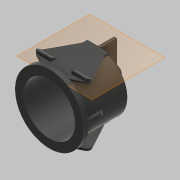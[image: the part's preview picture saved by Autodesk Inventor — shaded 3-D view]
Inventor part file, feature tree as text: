
AUTODESK INVENTOR PART (.ipt)
format: ipt  version: 2018.1 (Build 221171000, 171)  size: 242,688 bytes
history: native  units: mm
features: extrude x7, sketch x7, chamfer x3, other x2, mirror x1, projected_geometry x1
ambient origin geometry x8: Origin, YZ Plane, XZ Plane, XY Plane, X Axis, Y Axis, Z Axis, Center Point
bodies: body (feature_tree)
feature tree (21):
  other  "Твердое тело1"
  extrude  "Выдавливание1"  Depth=23.5mm
  extrude  "Выдавливание2"  Depth=18.0mm TaperAngle=0.0deg
  extrude  "Выдавливание3"  Depth=28.0mm
  extrude  "Выдавливание4"  Depth=2.0mm TaperAngle=0.0deg
  extrude  "Выдавливание5"  Depth=5.0mm
  chamfer  "Фаска1"  Distance=1.2mm
  other  "РабПлоскость1"
  extrude  "Выдавливание6"  Depth=2.5mm
  mirror  "Зеркальное отражение1"
  extrude  "Выдавливание8"  Depth=7.0mm TaperAngle=0.0deg
  chamfer  "Фаска2"  Distance=5.8mm
  chamfer  "Фаска3"  Distance=7.0mm
  sketch  "Эскиз1"
  sketch  "Эскиз2"
  sketch  "Эскиз3"
  sketch  "Эскиз4"
  sketch  "Эскиз5"
  sketch  "Эскиз7"
  sketch  "Эскиз9"
  projected_geometry  "Спроецированная петля1"
